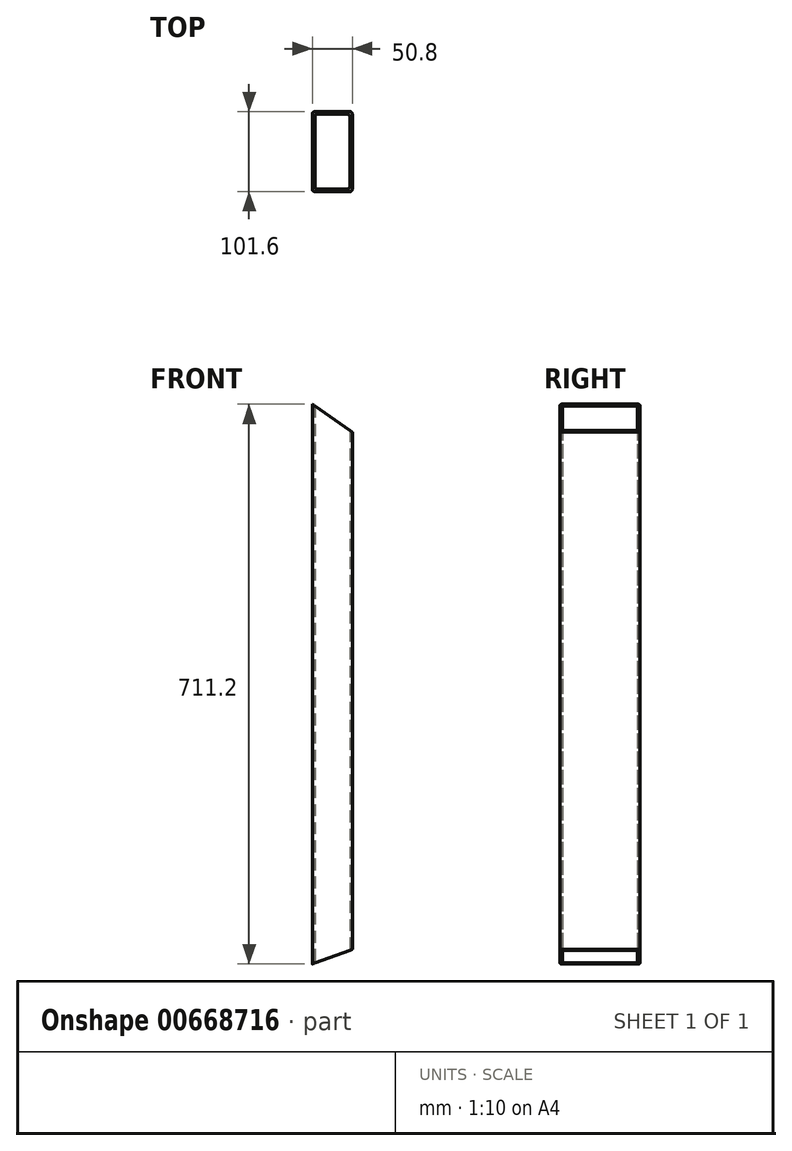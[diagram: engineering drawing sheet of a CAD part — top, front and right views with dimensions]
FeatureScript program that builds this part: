
annotation { "Feature Type Name" : "Feature", "Feature Type Description" : "" }
export const myFeature = defineFeature(function(context is Context, id is Id, definition is map)
    precondition{}
    {
        {
            var Q0;
            Q0=qCreatedBy(makeId("Top.planeOp"),FACE);
            var sketch = newSketch(context, id + "F0", { "sketchPlane" : qUnion([Q0])});
            skLineSegment(sketch, "E0.bottom", {"start": v(22.23, -50.8) * mm, "end": v(-22.22, -50.8) * mm});
            skLineSegment(sketch, "E0.top", {"start": v(22.22, 50.8) * mm, "end": v(-22.23, 50.8) * mm});
            skLineSegment(sketch, "E0.left", {"start": v(25.4, -47.62) * mm, "end": v(25.4, 47.63) * mm});
            skLineSegment(sketch, "E0.right", {"start": v(-25.4, -47.62) * mm, "end": v(-25.4, 47.63) * mm});
            skPoint(sketch, "E0.middle", {"position": v(0, 0) * mm});
            skLineSegment(sketch, "E1.bottom", {"start": v(19.05, -47.62) * mm, "end": v(-19.05, -47.63) * mm});
            skLineSegment(sketch, "E1.top", {"start": v(19.05, 47.63) * mm, "end": v(-19.05, 47.62) * mm});
            skLineSegment(sketch, "E1.left", {"start": v(22.23, -44.45) * mm, "end": v(22.22, 44.45) * mm});
            skLineSegment(sketch, "E1.right", {"start": v(-22.22, -44.45) * mm, "end": v(-22.23, 44.45) * mm});
            skPoint(sketch, "E2.visualSharp", {"position": v(-22.23, 47.62) * mm});
            skArc(sketch, "E2.filletArc", {"start": v(-19.05, 47.62) * mm, "mid": v(-21.3, 46.7) * mm, "end": v(-22.23, 44.45) * mm});
            skPoint(sketch, "E3.visualSharp", {"position": v(-25.4, 50.8) * mm});
            skArc(sketch, "E3.filletArc", {"start": v(-22.23, 50.8) * mm, "mid": v(-24.47, 49.87) * mm, "end": v(-25.4, 47.63) * mm});
            skPoint(sketch, "E4.visualSharp", {"position": v(22.22, 47.63) * mm});
            skArc(sketch, "E4.filletArc", {"start": v(22.22, 44.45) * mm, "mid": v(21.3, 46.7) * mm, "end": v(19.05, 47.63) * mm});
            skPoint(sketch, "E5.visualSharp", {"position": v(25.4, 50.8) * mm});
            skArc(sketch, "E5.filletArc", {"start": v(25.4, 47.63) * mm, "mid": v(24.47, 49.87) * mm, "end": v(22.22, 50.8) * mm});
            skPoint(sketch, "E6.visualSharp", {"position": v(-22.22, -47.63) * mm});
            skArc(sketch, "E6.filletArc", {"start": v(-22.22, -44.45) * mm, "mid": v(-21.3, -46.7) * mm, "end": v(-19.05, -47.63) * mm});
            skPoint(sketch, "E7.visualSharp", {"position": v(22.23, -47.62) * mm});
            skArc(sketch, "E7.filletArc", {"start": v(19.05, -47.62) * mm, "mid": v(21.3, -46.7) * mm, "end": v(22.23, -44.45) * mm});
            skPoint(sketch, "E8.visualSharp", {"position": v(25.4, -50.8) * mm});
            skArc(sketch, "E8.filletArc", {"start": v(22.23, -50.8) * mm, "mid": v(24.47, -49.87) * mm, "end": v(25.4, -47.62) * mm});
            skPoint(sketch, "E9.visualSharp", {"position": v(-25.4, -50.8) * mm});
            skArc(sketch, "E9.filletArc", {"start": v(-25.4, -47.62) * mm, "mid": v(-24.47, -49.87) * mm, "end": v(-22.22, -50.8) * mm});
            skSolve(sketch);
        }
        {
            var Q0;
            Q0=qSketchRegion(id+"F0",true);
            extrude(context, id + "F1", {"entities" : qUnion([Q0]), "depth" : 711.2 * mm});
        }
        {
            var Q0;
            Q0=qCreatedBy(makeId("Front.planeOp"),FACE);
            var sketch = newSketch(context, id + "F2", { "sketchPlane" : qUnion([Q0])});
            skLineSegment(sketch, "E10", {"start": v(-25.4, 0) * mm, "end": v(25.4, 18.49) * mm});
            skLineSegment(sketch, "E11", {"start": v(25.4, 18.49) * mm, "end": v(25.4, 0) * mm});
            skLineSegment(sketch, "E12", {"start": v(25.4, 0) * mm, "end": v(-25.4, 0) * mm});
            skSolve(sketch);
        }
        {
            var Q0;
            Q0=qSketchRegion(id+"F2",true);
            extrude(context, id + "F3", {"entities" : qUnion([Q0]), "operationType" : NewBodyOperationType.REMOVE, "endBound" : BoundingType.THROUGH_ALL, "oppositeDirection" : true, "depth" : 25.4 * mm, "hasSecondDirection" : true, "secondDirectionBound" : SecondDirectionBoundingType.THROUGH_ALL, "secondDirectionOppositeDirection" : false, "secondDirectionDepth" : 25.4 * mm});
        }
        {
            var Q0;
            Q0=qCreatedBy(makeId("Front.planeOp"),FACE);
            var sketch = newSketch(context, id + "F4", { "sketchPlane" : qUnion([Q0])});
            skLineSegment(sketch, "E13", {"start": v(-25.4, 711.2) * mm, "end": v(25.4, 675.63) * mm});
            skLineSegment(sketch, "E14", {"start": v(25.4, 675.63) * mm, "end": v(25.4, 711.2) * mm});
            skLineSegment(sketch, "E15", {"start": v(25.4, 711.2) * mm, "end": v(-25.4, 711.2) * mm});
            skSolve(sketch);
        }
        {
            var Q0;
            Q0=qSketchRegion(id+"F4",true);
            extrude(context, id + "F5", {"entities" : qUnion([Q0]), "operationType" : NewBodyOperationType.REMOVE, "endBound" : BoundingType.THROUGH_ALL, "oppositeDirection" : true, "depth" : 25.4 * mm, "hasSecondDirection" : true, "secondDirectionBound" : SecondDirectionBoundingType.THROUGH_ALL, "secondDirectionOppositeDirection" : false, "secondDirectionDepth" : 25.4 * mm});
        }
    });
